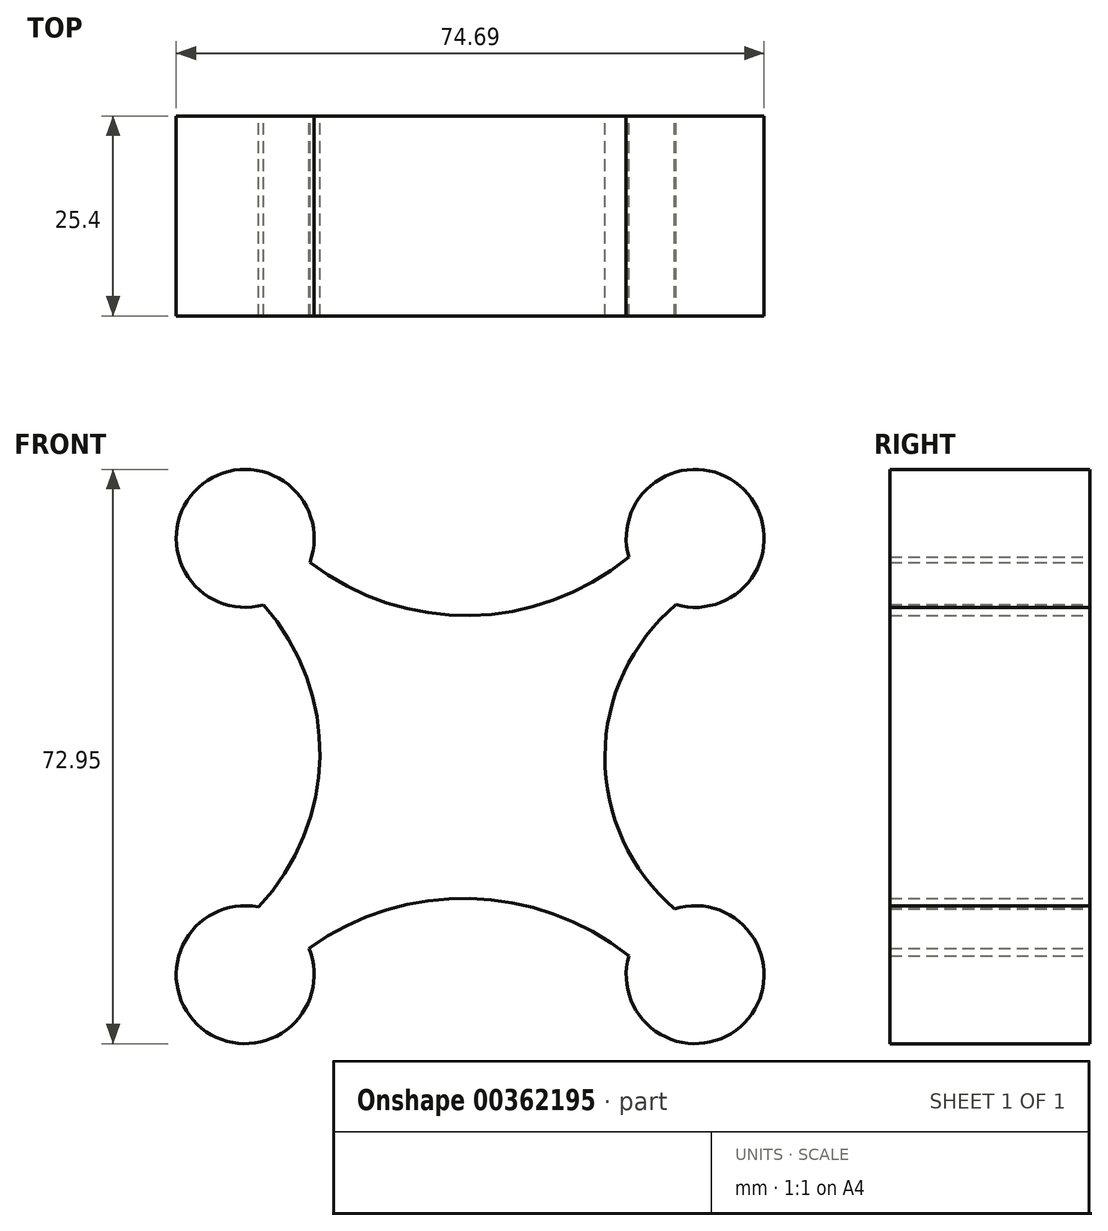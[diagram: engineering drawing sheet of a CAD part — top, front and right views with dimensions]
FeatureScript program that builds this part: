
annotation { "Feature Type Name" : "Feature", "Feature Type Description" : "" }
export const myFeature = defineFeature(function(context is Context, id is Id, definition is map)
    precondition{}
    {
        {
            var Q0;
            Q0=qCreatedBy(makeId("Front.planeOp"),FACE);
            var sketch = newSketch(context, id + "F0", { "sketchPlane" : qUnion([Q0])});
            skCircle(sketch, "E0", {"center": v(-26.95, 25.77) * mm, "radius": 8.76 * mm});
            skCircle(sketch, "E1", {"center": v(-26.95, -29.66) * mm, "radius": 8.76 * mm});
            skCircle(sketch, "E2", {"center": v(30.2, 25.77) * mm, "radius": 8.76 * mm});
            skCircle(sketch, "E3", {"center": v(30.2, -29.66) * mm, "radius": 8.76 * mm});
            skArc(sketch, "E4", {"start": v(-18.74, 22.73) * mm, "mid": v(1.63, 15.98) * mm, "end": v(21.78, 23.37) * mm});
            skArc(sketch, "E5", {"start": v(27.79, 17.35) * mm, "mid": v(18.74, -1.93) * mm, "end": v(27.59, -21.3) * mm});
            skArc(sketch, "E6", {"start": v(21.78, -27.26) * mm, "mid": v(1.62, -19.98) * mm, "end": v(-18.86, -26.3) * mm});
            skArc(sketch, "E7", {"start": v(-25.28, -21.06) * mm, "mid": v(-17.47, -2) * mm, "end": v(-24.61, 17.33) * mm});
            skSolve(sketch);
        }
        {
            var Q0;
            Q0 = qSketchRegion(id + "F0", true);
            extrude(context, id + "F1", {"entities" : qUnion([Q0]), "depth" : 25.4 * mm});
        }
    });
